# Revit family: SE-SU-800_GENERADO
name_source: partatom
category: Equipos mecánicos
revit_build: Autodesk Revit 2014 (Build: 20130308_1515(x64)
units: mm (PartAtom-declared; Revit-internal decimal feet)

## types (52) — shared parameters
Depth = 757 mm  [stored 2.4836 ft]
Fabricante = SAMMIC S.L.
Foodservice Equipment Identifier = Sí
Height = 998 mm  [stored 3.27428 ft]
Revision Code = 1
URL = https://www.sammic.com
URL Cutsheet = http://www.sammic.com
Width = 960 mm  [stored 3.14961 ft]

## per-type parameters (varying)
| type | Comentarios de tipo | Cycle | FL Amps | HP | Modelo | Specification by Manufacturer | Volts | Watts | Weight in Pounds |
| Vacuum packing machine SE-806 230-400/50/3N | Floorstanding unit. 63 m³/h. 530+848 mm.

ELECTRICAL DATA:

230V/50Hz/3~ (10.2A) | 50 Hz | 7 A | 4.02 | 1140680 | Two sealing bars (530+848 mm.)
63 m³/h Busch vacuum pump.
Vacuum controlled by sensor. | 400 V | 3000 W | 511.5 |
| Vacuum packing machine SE-806 208-240V/60/3 | Floorstanding unit. 63 m³/h. 530+848 mm.

ELECTRICAL DATA:

230V/60Hz/3~ (8.2A) | 60 Hz | 8 A | 5.23 | 1140688 | Two sealing bars (530+848 mm.)
63 m³/h Busch vacuum pump.
Vacuum controlled by sensor. | 208 V | 3900 W | 511.5 |
| Vacuum packing machine SE-806 220/60/3 | Floorstanding unit. 63 m³/h. 530+848 mm. | 60 Hz | 10 A | 4.96 | 1140712 | Two sealing bars (530+848 mm.)
63 m³/h Busch vacuum pump.
Vacuum controlled by sensor. | 220 V | 3700 W | 511.5 |
| Vacuum packing machine SE-806 CC 230-400/50/3N | Floorstanding unit. 63 m³/h. 581+581 mm.

ELECTRICAL DATA:

230V/50Hz/3~ (10.2A) | 50 Hz | 7 A | 3.62 | 1140681 | Two sealing bars (581+581 mm.)
63 m³/h Busch vacuum pump.
Vacuum controlled by sensor. | 400 V | 2700 W | 511.5 |
| Vacuum packing machine SE-806 CC 208-240V/60/3 | Floorstanding unit. 63 m³/h. 581+581 mm.

ELECTRICAL DATA:

230V/60Hz/3~ (8.2A) | 60 Hz | 8 A | 4.83 | 1140689 | Two sealing bars (581+581 mm.)
63 m³/h Busch vacuum pump.
Vacuum controlled by sensor. | 208 V | 3600 W | 511.5 |
| Vacuum packing machine SE-806 LL 230-400/50/3N | Floorstanding unit. 63 m³/h. 848+848 mm.

ELECTRICAL DATA:

230V/50Hz/3~ (10.2A) | 50 Hz | 7 A | 4.43 | 1140682 | Two sealing bars (848+848 mm.)
63 m³/h Busch vacuum pump.
Vacuum controlled by sensor. | 400 V | 3300 W | 511.5 |
| Vacuum packing machine SE-806 LL 208-240V/60/3 | Floorstanding unit. 63 m³/h. 848+848 mm.

ELECTRICAL DATA:

230V/60Hz/3~ (8.2A) | 60 Hz | 8 A | 5.63 | 1140690 | Two sealing bars (848+848 mm.)
63 m³/h Busch vacuum pump.
Vacuum controlled by sensor. | 208 V | 4200 W | 511.5 |
| Vacuum packing machine SE-806 LL 400/60/3N | Floorstanding unit. 63 m³/h. 848+848 mm. | 0 Hz | 0 A |  | 1140686 | Two sealing bars (848+848 mm.)
63 m³/h Busch vacuum pump.
Vacuum controlled by sensor. | 0 V | 0 W | 511.5 |
| Vacuum packing machine SE-810 400/50-60/3N | Floorstanding unit. 100 m³/h. 530+848 mm. | 50 Hz | 9 A | 4.96 | 1140696 | Two sealing bars (530+848 mm.)
100 m³/h Busch vacuum pump.
Vacuum controlled by sensor. | 400 V | 3700 W | 551.2 |
| Vacuum packing machine SE-810 208-240V/60/3 | Floorstanding unit. 100 m³/h. 530+848 mm.

ELECTRICAL DATA:

230V/60Hz/3~ (12.8A) | 60 Hz | 13 A | 6.57 | 1140704 | Two sealing bars (530+848 mm.)
100 m³/h Busch vacuum pump.
Vacuum controlled by sensor. | 208 V | 4900 W | 551.2 |
| Vacuum packing machine SE-810 CC 400/50-60/3N | Floorstanding unit. 100 m³/h. 581+581 mm. | 50 Hz | 9 A | 4.56 | 1140697 | Two sealing bars (581+581 mm.)
100 m³/h Busch vacuum pump.
Vacuum controlled by sensor. | 400 V | 3400 W | 551.2 |
| Vacuum packing machine SE-810 CC 208-240V/60/3 | Floorstanding unit. 100 m³/h. 581+581 mm.

ELECTRICAL DATA:

230V/60Hz/3~ (12.8A) | 60 Hz | 13 A | 6.3 | 1140705 | Two sealing bars (581+581 mm.)
100 m³/h Busch vacuum pump.
Vacuum controlled by sensor. | 208 V | 4700 W | 551.2 |
| Vacuum packing machine SE-810 LL 400/50-60/3N | Floorstanding unit. 100 m³/h. 848+848 mm. | 50 Hz | 9 A | 5.36 | 1140698 | Two sealing bars (848+848 mm.)
63 m³/h Busch vacuum pump.
Vacuum controlled by sensor. | 400 V | 4000 W | 551.2 |
| Vacuum packing machine SE-810 LL 208-240V/60/3 | Floorstanding unit. 100 m³/h. 848+848 mm.

ELECTRICAL DATA:

230V/60Hz/3~ (12.8A) | 60 Hz | 13 A | 6.97 | 1140706 | Two sealing bars (848+848 mm.)
63 m³/h Busch vacuum pump.
Vacuum controlled by sensor. | 208 V | 5200 W | 551.2 |
| Vacuum packing machine SU-806 230-400/50/3N | Floorstanding unit. 63 m³/h. 530+848 mm.

ELECTRICAL DATA:

230V/50Hz/3~ (9.5A) | 50 Hz | 6 A | 4.02 | 1140881 | Two sealing bars (530+848 mm.)
63 m³/h Busch vacuum pump.
Vacuum controlled by sensor. | 400 V | 3000 W | 511.5 |
| Vacuum packing machine SU-806P 230-400/50/3N | Floorstanding unit. 63 m³/h. 530+848 mm.

ELECTRICAL DATA:

230V/50Hz/3~ (9.5A) | 50 Hz | 6 A | 4.02 | 1140884 | Two sealing bars (530+848 mm.)
63 m³/h Busch vacuum pump.
Vacuum controlled by sensor. | 400 V | 3000 W | 511.5 |
| Vacuum packing machine SU-806 208-240/60/3 | Floorstanding unit. 63 m³/h. 530+848 mm.

ELECTRICAL DATA:

230V/60Hz/3~ (8.2A) | 60 Hz | 8 A | 5.23 | 1140899 | Two sealing bars (530+848 mm.)
63 m³/h Busch vacuum pump.
Vacuum controlled by sensor. | 208 V | 3900 W | 511.5 |
| Vacuum packing machine SU-806P 208-240/60/3 | Floorstanding unit. 63 m³/h. 530+848 mm.

ELECTRICAL DATA:

230V/60Hz/3~ (8.2A) | 60 Hz | 8 A | 5.23 | 1140902 | Two sealing bars (530+848 mm.)
63 m³/h Busch vacuum pump.
Vacuum controlled by sensor. | 208 V | 3900 W | 511.5 |
| Vacuum packing machine SU-806 CC 230-400/50/3N | Floorstanding unit. 63 m³/h. 581+581 mm.

ELECTRICAL DATA:

230V/50Hz/3~ (9.5A) | 50 Hz | 6 A | 3.62 | 1140887 | Two sealing bars (581+581 mm.)
63 m³/h Busch vacuum pump.
Vacuum controlled by sensor. | 400 V | 2700 W | 511.5 |
| Vacuum packing machine SU-806P CC 230-400/50/3N | Floorstanding unit. 63 m³/h. 581+581 mm.

ELECTRICAL DATA:

230V/50Hz/3~ (9.5A) | 50 Hz | 6 A | 3.62 | 1140890 | Two sealing bars (581+581 mm.)
63 m³/h Busch vacuum pump.
Vacuum controlled by sensor. | 400 V | 2700 W | 511.5 |
| Vacuum packing machine SU-806 CC 208-240/60/3 | Floorstanding unit. 63 m³/h. 581+581 mm.

ELECTRICAL DATA:

230V/60Hz/3~ (8.2A) | 60 Hz | 8 A | 4.83 | 1140905 | Two sealing bars (581+581 mm.)
63 m³/h Busch vacuum pump.
Vacuum controlled by sensor. | 208 V | 3600 W | 511.5 |
| Vacuum packing machine SU-806P CC 208-240/60/3 | Floorstanding unit. 63 m³/h. 581+581 mm.

ELECTRICAL DATA:

230V/60Hz/3~ (8.2A) | 60 Hz | 8 A | 4.83 | 1140908 | Two sealing bars (581+581 mm.)
63 m³/h Busch vacuum pump.
Vacuum controlled by sensor. | 208 V | 3600 W | 511.5 |
| Vacuum packing machine SU-806 LL 230-400/50/3N | Floorstanding unit. 63 m³/h. 848+848 mm.

ELECTRICAL DATA:

230V/50Hz/3~ (9.5A) | 50 Hz | 6 A | 4.43 | 1140893 | Two sealing bars (848+848 mm)
63 m³/h Busch vacuum pump.
Vacuum controlled by sensor. | 400 V | 3300 W | 511.5 |
| Vacuum packing machine SU-806P LL 230-400/50/3N | Floorstanding unit. 63 m³/h. 848+848 mm.

ELECTRICAL DATA:

230V/50Hz/3~ (9.5A) | 50 Hz | 6 A | 4.43 | 1140896 | Two sealing bars (848+848 mm)
63 m³/h Busch vacuum pump.
Vacuum controlled by sensor. | 400 V | 3300 W | 511.5 |
| Vacuum packing machine SU-806 LL 208-240/60/3 | Floorstanding unit. 63 m³/h. 848+848 mm.

ELECTRICAL DATA:

230V/60Hz/3~ (8.2A) | 60 Hz | 8 A | 5.63 | 1140911 | Two sealing bars (848+848 mm)
63 m³/h Busch vacuum pump.
Vacuum controlled by sensor. | 208 V | 4200 W | 511.5 |
| Vacuum packing machine SU-806P LL 208-240/60/3 | Floorstanding unit. 63 m³/h. 848+848 mm.

ELECTRICAL DATA:

230V/60Hz/3~ (8.2A) | 60 Hz | 8 A | 5.63 | 1140914 | Two sealing bars (848+848 mm)
63 m³/h Busch vacuum pump.
Vacuum controlled by sensor. | 208 V | 4200 W | 511.5 |
| Vacuum packing machine SU-806 LL 220/60/3 | Floorstanding unit. 63 m³/h. 848+848 mm. | 60 Hz | 10 A | 4.43 | 1140929 | Two sealing bars (848+848 mm)
63 m³/h Busch vacuum pump.
Vacuum controlled by sensor. | 220 V | 3300 W | 511.5 |
| Vacuum packing machine SU-810 400/50-60/3N | Floorstanding unit. 100m³/h. 530+848 mm. | 50 Hz | 8 A | 4.96 | 1140935 | Two sealing bars (530+848 mm.)
100 m³/h Busch vacuum pump.
Vacuum controlled by sensor. | 400 V | 3700 W | 551.2 |
| Vacuum packing machine SU-810P 400/50-60/3N | Floorstanding unit. 100m³/h. 530+848 mm. | 50 Hz | 8 A | 4.96 | 1140938 | Two sealing bars (530+848 mm.)
100 m³/h Busch vacuum pump.
Vacuum controlled by sensor. | 400 V | 3700 W | 551.2 |
| Vacuum packing machine SU-810+ 400/50-60/3N | Floorstanding unit. 100m³/h. 530+848 mm. | 50 Hz | 8 A | 4.96 | 1140939 | Two sealing bars (530+848 mm.)
100 m³/h Busch vacuum pump.
Vacuum controlled by sensor. | 400 V | 3700 W | 551.2 |
| Vacuum packing machine SU-810P+ 400/50-60/3N | Floorstanding unit. 100m³/h. 530+848 mm. | 50 Hz | 8 A | 4.96 | 1140940 | Two sealing bars (530+848 mm.)
100 m³/h Busch vacuum pump.
Vacuum controlled by sensor. | 400 V | 3700 W | 551.2 |
| Vacuum packing machine SU-810 208-240/60/3 | Floorstanding unit. 100m³/h. 530+848 mm.

ELECTRICAL DATA:

230V/60Hz/3~ (12.8A) | 60 Hz | 13 A | 6.57 | 1140965 | Two sealing bars (530+848 mm.)
100 m³/h Busch vacuum pump.
Vacuum controlled by sensor. | 208 V | 4900 W | 551.2 |
| Vacuum packing machine SU-810P 208-240/60/3 | Floorstanding unit. 100m³/h. 530+848 mm.

ELECTRICAL DATA:

230V/60Hz/3~ (12.8A) | 60 Hz | 13 A | 6.57 | 1140968 | Two sealing bars (530+848 mm.)
100 m³/h Busch vacuum pump.
Vacuum controlled by sensor. | 208 V | 4900 W | 551.2 |
| Vacuum packing machine SU-810+ 208-240/60/3 | Floorstanding unit. 100m³/h. 530+848 mm.

ELECTRICAL DATA:

230V/60Hz/3~ (12.8A) | 60 Hz | 13 A | 6.57 | 1140969 | Two sealing bars (530+848 mm.)
100 m³/h Busch vacuum pump.
Vacuum controlled by sensor. | 208 V | 4900 W | 551.2 |
| Vacuum packing machine SU-810P+ 208-240/60/3 | Floorstanding unit. 100m³/h. 530+848 mm.

ELECTRICAL DATA:

230V/60Hz/3~ (12.8A) | 60 Hz | 13 A | 6.57 | 1140970 | Two sealing bars (530+848 mm.)
100 m³/h Busch vacuum pump.
Vacuum controlled by sensor. | 208 V | 4900 W | 551.2 |
| Vacuum packing machine SU-810 CC 400/50-60/3N | Floorstanding unit. 100m³/h. 581+581 mm. | 50 Hz | 8 A | 4.56 | 1140945 | Two sealing bars (581+581 mm.)
100 m³/h Busch vacuum pump.
Vacuum controlled by sensor. | 400 V | 3400 W | 551.2 |
| Vacuum packing machine SU-810P CC 400/50-60/3N | Floorstanding unit. 100m³/h. 581+581 mm. | 50 Hz | 8 A | 4.56 | 1140948 | Two sealing bars (581+581 mm.)
100 m³/h Busch vacuum pump.
Vacuum controlled by sensor. | 400 V | 3400 W | 551.2 |
| Vacuum packing machine SU-810+ CC 400/50-60/3N | Floorstanding unit. 100m³/h. 581+581 mm. | 50 Hz | 8 A | 4.56 | 1140949 | Two sealing bars (581+581 mm.)
100 m³/h Busch vacuum pump.
Vacuum controlled by sensor. | 400 V | 3400 W | 551.2 |
| Vacuum packing machine SU-810P+ CC 400/50-60/3N | Floorstanding unit. 100m³/h. 581+581 mm. | 50 Hz | 8 A | 4.56 | 1140950 | Two sealing bars (581+581 mm.)
100 m³/h Busch vacuum pump.
Vacuum controlled by sensor. | 400 V | 3400 W | 551.2 |
| Vacuum packing machine SU-810 CC 208-240/60/3 | Floorstanding unit. 100m³/h. 581+581 mm.

ELECTRICAL DATA:

230V/60Hz/3~ (12.8A) | 60 Hz | 13 A | 6.17 | 1140975 | Two sealing bars (581+581 mm.)
100 m³/h Busch vacuum pump.
Vacuum controlled by sensor. | 208 V | 4600 W | 551.2 |
| Vacuum packing machine SU-810P CC 208-240/60/3 | Floorstanding unit. 100m³/h. 581+581 mm.

ELECTRICAL DATA:

230V/60Hz/3~ (12.8A) | 60 Hz | 13 A | 6.17 | 1140978 | Two sealing bars (581+581 mm.)
100 m³/h Busch vacuum pump.
Vacuum controlled by sensor. | 208 V | 4600 W | 551.2 |
| Vacuum packing machine SU-810+ CC 208-240/60/3 | Floorstanding unit. 100m³/h. 581+581 mm.

ELECTRICAL DATA:

230V/60Hz/3~ (12.8A) | 60 Hz | 13 A | 6.17 | 1140979 | Two sealing bars (581+581 mm.)
100 m³/h Busch vacuum pump.
Vacuum controlled by sensor. | 208 V | 4600 W | 551.2 |
| Vacuum packing machine SU-810P+ CC 208-240/60/3 | Floorstanding unit. 100m³/h. 581+581 mm.

ELECTRICAL DATA:

230V/60Hz/3~ (12.8A) | 60 Hz | 13 A | 6.17 | 1140980 | Two sealing bars (581+581 mm.)
100 m³/h Busch vacuum pump.
Vacuum controlled by sensor. | 208 V | 4600 W | 551.2 |
| Vacuum packing machine SU-810 LL 400/50-60/3N | Floorstanding unit. 100m³/h. 848+848 mm. | 50 Hz | 8 A | 5.36 | 1140955 | Two sealing bars (848+848 mm.)
100 m³/h Busch vacuum pump.
Vacuum controlled by sensor. | 400 V | 4000 W | 551.2 |
| Vacuum packing machine SU-810P LL 400/50-60/3N | Floorstanding unit. 100m³/h. 848+848 mm. | 50 Hz | 8 A | 5.36 | 1140958 | Two sealing bars (848+848 mm.)
100 m³/h Busch vacuum pump.
Vacuum controlled by sensor. | 400 V | 4000 W | 551.2 |
| Vacuum packing machine SU-810+ LL 400/50-60/3N | Floorstanding unit. 100m³/h. 848+848 mm. | 50 Hz | 8 A | 5.36 | 1140959 | Two sealing bars (848+848 mm.)
100 m³/h Busch vacuum pump.
Vacuum controlled by sensor. | 400 V | 4000 W | 551.2 |
| Vacuum packing machine SU-810P+ LL 400/50-60/3N | Floorstanding unit. 100m³/h. 848+848 mm. | 50 Hz | 8 A | 5.36 | 1140960 | Two sealing bars (848+848 mm.)
100 m³/h Busch vacuum pump.
Vacuum controlled by sensor. | 400 V | 4000 W | 551.2 |
| Vacuum packing machine SU-810 LL 208-240/60/3 | Floorstanding unit. 100m³/h. 848+848 mm.

ELECTRICAL DATA:

230V/60Hz/3~ (12.8A) | 60 Hz | 13 A | 6.97 | 1140985 | Two sealing bars (848+848 mm.)
100 m³/h Busch vacuum pump.
Vacuum controlled by sensor. | 208 V | 5200 W | 551.2 |
| Vacuum packing machine SU-810P LL 208-240/60/3 | Floorstanding unit. 100m³/h. 848+848 mm.

ELECTRICAL DATA:

230V/60Hz/3~ (12.8A) | 60 Hz | 13 A | 6.97 | 1140988 | Two sealing bars (848+848 mm.)
100 m³/h Busch vacuum pump.
Vacuum controlled by sensor. | 208 V | 5200 W | 551.2 |
| Vacuum packing machine SU-810+ LL 208-240/60/3 | Floorstanding unit. 100m³/h. 848+848 mm.

ELECTRICAL DATA:

230V/60Hz/3~ (12.8A) | 60 Hz | 13 A | 6.97 | 1140989 | Two sealing bars (848+848 mm.)
100 m³/h Busch vacuum pump.
Vacuum controlled by sensor. | 208 V | 5200 W | 551.2 |
| Vacuum packing machine SU-810P+ LL 208-240/60/3 | Floorstanding unit. 100m³/h. 848+848 mm.

ELECTRICAL DATA:

230V/60Hz/3~ (12.8A) | 60 Hz | 13 A | 6.97 | 1140990 | Two sealing bars (848+848 mm.)
100 m³/h Busch vacuum pump.
Vacuum controlled by sensor. | 208 V | 5200 W | 551.2 |
| Vacuum packing machine SU-810+ LL 220/60/3 | Floorstanding unit. 100m³/h. 848+848 mm. | 60 Hz | 15 A | 6.97 | 1141020 | Two sealing bars (848+848 mm.)
100 m³/h Busch vacuum pump.
Vacuum controlled by sensor. | 220 V | 5200 W | 551.2 |

note: column(s) folded — value = type name in every type: Descripción

note: [stored X ft] marks values corroborated as IEEE doubles in the binary element streams (Revit-internal decimal feet)
